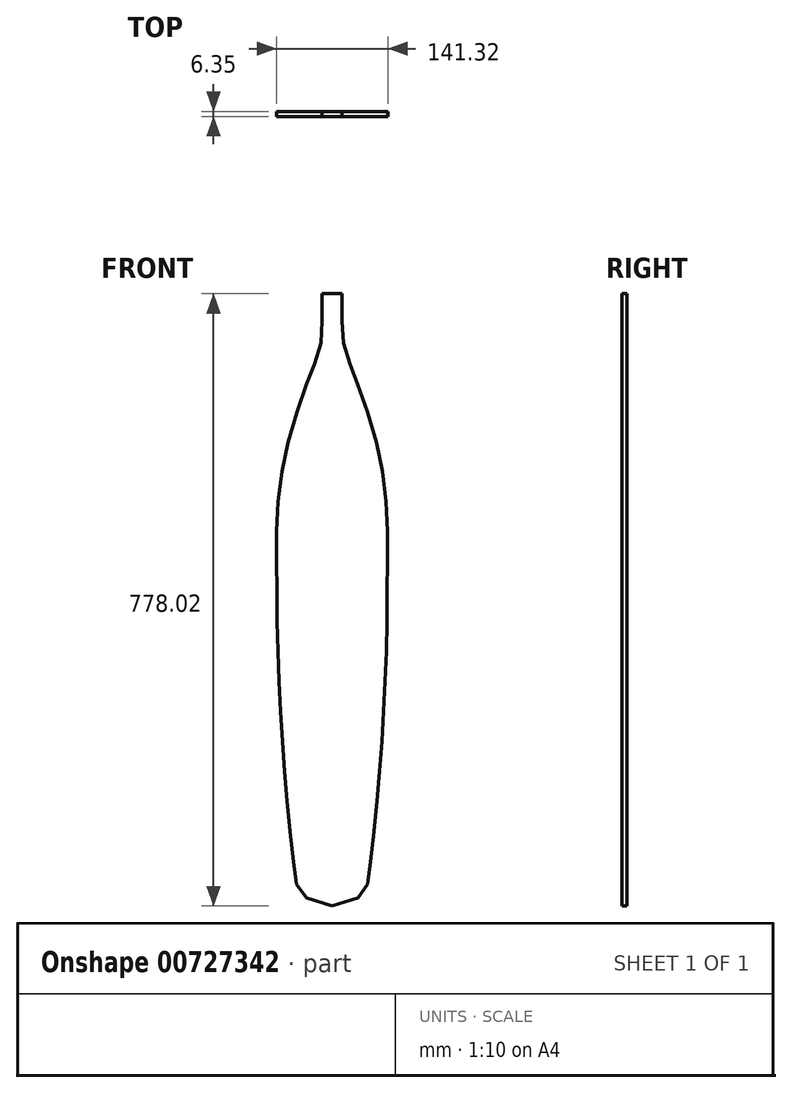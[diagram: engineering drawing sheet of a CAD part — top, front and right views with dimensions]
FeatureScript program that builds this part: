
annotation { "Feature Type Name" : "Feature", "Feature Type Description" : "" }
export const myFeature = defineFeature(function(context is Context, id is Id, definition is map)
    precondition{}
    {
        {
            var Q0;
            Q0=qCreatedBy(makeId("Front.planeOp"),FACE);
            var sketch = newSketch(context, id + "F0", { "sketchPlane" : qUnion([Q0])});
            skPoint(sketch, "E0", {"position": v(0, 0) * mm});
            skPoint(sketch, "E1", {"position": v(35.72, 12.7) * mm});
            skPoint(sketch, "E2", {"position": v(44.45, 25.4) * mm});
            skPoint(sketch, "E3", {"position": v(48.42, 50.8) * mm});
            skPoint(sketch, "E4", {"position": v(53.98, 101.6) * mm});
            skPoint(sketch, "E5", {"position": v(58.74, 152.4) * mm});
            skPoint(sketch, "E6", {"position": v(62.7, 203.2) * mm});
            skPoint(sketch, "E7", {"position": v(65.88, 254) * mm});
            skPoint(sketch, "E8", {"position": v(68.26, 304.8) * mm});
            skPoint(sketch, "E9", {"position": v(69.85, 355.6) * mm});
            skPoint(sketch, "E10", {"position": v(69.85, 406.4) * mm});
            skPoint(sketch, "E11", {"position": v(70.64, 457.2) * mm});
            skPoint(sketch, "E12", {"position": v(69.06, 508) * mm});
            skPoint(sketch, "E13", {"position": v(62.7, 558.8) * mm});
            skPoint(sketch, "E14", {"position": v(50.8, 609.6) * mm});
            skPoint(sketch, "E15", {"position": v(33.34, 660.4) * mm});
            skPoint(sketch, "E16", {"position": v(23.81, 685.8) * mm});
            skPoint(sketch, "E17", {"position": v(15.08, 711.2) * mm});
            skPoint(sketch, "E18", {"position": v(12.7, 736.6) * mm});
            skFitSpline(sketch, "E19", {"points": [v(0, 0) * mm, v(35.72, 12.7) * mm, v(44.45, 25.4) * mm, v(48.42, 50.8) * mm, v(53.98, 101.6) * mm, v(58.74, 152.4) * mm, v(62.7, 203.2) * mm, v(65.88, 254) * mm, v(68.26, 304.8) * mm, v(69.85, 355.6) * mm, v(69.85, 406.4) * mm, v(70.64, 457.2) * mm, v(69.06, 508) * mm, v(62.7, 558.8) * mm, v(50.8, 609.6) * mm, v(33.34, 660.4) * mm, v(23.81, 685.8) * mm, v(15.08, 711.2) * mm, v(12.7, 736.6) * mm, v(12.7, 778.02) * mm], "startDerivative": vector(1031.9, 0) * mm, "endDerivative": vector(5.47, 842.7) * mm});
            skFitSpline(sketch, "E20.MirrorCS", {"points": [v(0, 0) * mm, v(-35.72, 12.7) * mm, v(-44.45, 25.4) * mm, v(-48.42, 50.8) * mm, v(-53.98, 101.6) * mm, v(-58.74, 152.4) * mm, v(-62.7, 203.2) * mm, v(-65.88, 254) * mm, v(-68.26, 304.8) * mm, v(-69.85, 355.6) * mm, v(-69.85, 406.4) * mm, v(-70.64, 457.2) * mm, v(-69.06, 508) * mm, v(-62.7, 558.8) * mm, v(-50.8, 609.6) * mm, v(-33.34, 660.4) * mm, v(-23.81, 685.8) * mm, v(-15.08, 711.2) * mm, v(-12.7, 736.6) * mm, v(-12.7, 778.02) * mm], "startDerivative": vector(-1031.9, 0) * mm, "endDerivative": vector(-5.47, 842.7) * mm});
            skLineSegment(sketch, "E21", {"start": v(-12.7, 778.02) * mm, "end": v(12.7, 778.02) * mm});
            skSolve(sketch);
        }
        {
            var Q0;
            Q0 = qSketchRegion(id + "F0", true);
            extrude(context, id + "F1", {"entities" : qUnion([Q0]), "depth" : 6.35 * mm, "offsetDistance" : 25.4 * mm});
        }
    });
